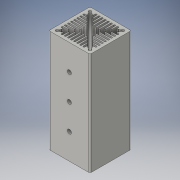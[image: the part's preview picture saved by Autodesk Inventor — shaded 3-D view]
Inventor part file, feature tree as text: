
AUTODESK INVENTOR PART (.ipt)
format: ipt  version: 2016 (Build 200138000, 138)  size: 506,368 bytes
history: native  units: mm
features: hole x1, sketch x1, other x1
ambient origin geometry x8: Origin, YZ Plane, XZ Plane, XY Plane, X Axis, Y Axis, Z Axis, Center Point
bodies: Solid1 (feature_tree)
feature tree (3):
  hole  "Hole1"  [1 undecoded]
  sketch  "Sketch1"  dims[d0=50.0mm d1=25.0mm d2=25.0mm d3=4.0mm d4=6.0mm d5=7.0mm d6=1.0mm d7=90.0deg d8=8.0mm d9=20.594885mm]
  other  "LAM_4"
note: 1 required parameter value undecoded (feature->parameter linkage not recoverable at this tier; creation-order binding heuristic only, values carry confidence <= 0.55)
